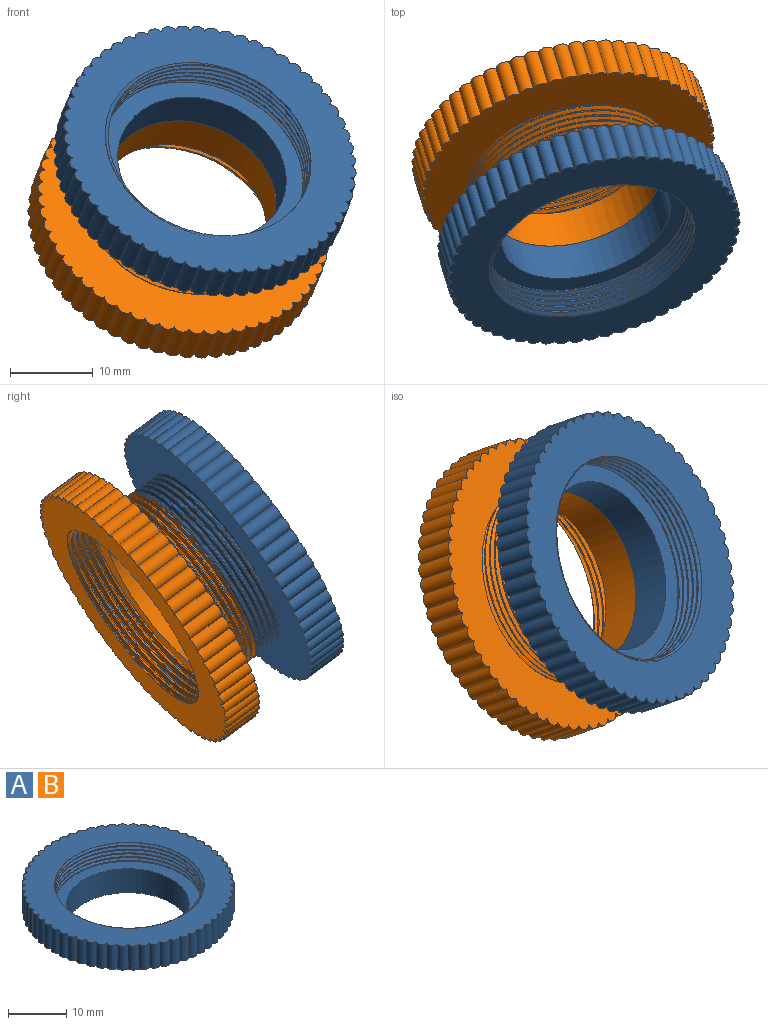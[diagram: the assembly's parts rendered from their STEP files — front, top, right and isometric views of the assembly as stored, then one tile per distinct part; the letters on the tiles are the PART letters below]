
ASSEMBLY  parts=2 mates=1
PART A: 73 faces, bbox 36.8x36.8x10.1 mm
  f0: plane 25.92x25.91mm, normal (0,0,1), area 167.9mm2, adj f4,f9,f10,f11,f12
  f1: plane 36.8x36.8mm, normal (0,0,1), area 507.3mm2, adj f9,f10,f11,f12,f13,f14,f15,f16
  f2: plane 24.63x24.59mm, normal (0,0,-1), area 117.6mm2, adj f3,f4,f6,f7,f8
  f3: cylinder r=12.4mm len=24.8mm, axis (0,0,-1), area 38.2mm2, adj f2,f5,f7,f8
  f4: cylinder r=10.5mm len=21mm, axis (0,0,-1), area 329.9mm2, adj f0,f2
  f5: plane 36.65x36.65mm, normal (0,0,-1), area 557.7mm2, adj f3,f6,f7,f8,f13,f14,f15,f16
  f6: bspline ~27.64x23.94mm, area 84.1mm2, adj f2,f5,f7,f8
  f7: bspline ~28.64x24.8mm, area 191.6mm2, adj f2,f3,f5,f6
  f8: bspline ~28.64x24.8mm, area 191.6mm2, adj f2,f3,f5,f6
  f9: bspline ~26.06x26.05mm, area 201.3mm2, adj f0,f1,f11,f12
  f10: bspline ~30.1x26.07mm, area 201.5mm2, adj f0,f1,f11,f12
  f11: bspline ~30.18x26.14mm, area 47.5mm2, adj f0,f1,f9,f10
  f12: cylinder r=12.6mm len=25.21mm, axis (0,0,1), area 81.8mm2, adj f0,f1,f9,f10
  f13: cylinder r=1mm len=5mm, axis (0,0,-1), area 11.7mm2, adj f1,f5,f14,f72
  f14: cylinder r=1mm len=5mm, axis (0,0,-1), area 11.7mm2, adj f1,f5,f13,f15
  f15: cylinder r=1mm len=5mm, axis (0,0,-1), area 11.7mm2, adj f1,f5,f14,f16
  f16: cylinder r=1mm len=5mm, axis (0,0,-1), area 11.7mm2, adj f1,f5,f15,f17
  f17: cylinder r=1mm len=5mm, axis (0,0,-1), area 11.7mm2, adj f1,f5,f16,f18
  f18: cylinder r=1mm len=5mm, axis (0,0,-1), area 11.7mm2, adj f1,f5,f17,f19
  f19: cylinder r=1mm len=5mm, axis (0,0,-1), area 11.7mm2, adj f1,f5,f18,f20
  f20: cylinder r=1mm len=5mm, axis (0,0,-1), area 11.7mm2, adj f1,f5,f19,f21
  f21: cylinder r=1mm len=5mm, axis (0,0,-1), area 11.7mm2, adj f1,f5,f20,f22
  f22: cylinder r=1mm len=5mm, axis (0,0,-1), area 11.7mm2, adj f1,f5,f21,f23
  f23: cylinder r=1mm len=5mm, axis (0,0,-1), area 11.7mm2, adj f1,f5,f22,f24
  f24: cylinder r=1mm len=5mm, axis (0,0,-1), area 11.7mm2, adj f1,f5,f23,f25
  f25: cylinder r=1mm len=5mm, axis (0,0,-1), area 11.7mm2, adj f1,f5,f24,f26
  f26: cylinder r=1mm len=5mm, axis (0,0,-1), area 11.7mm2, adj f1,f5,f25,f27
  f27: cylinder r=1mm len=5mm, axis (0,0,-1), area 11.7mm2, adj f1,f5,f26,f28
  f28: cylinder r=1mm len=5mm, axis (0,0,-1), area 11.7mm2, adj f1,f5,f27,f29
  f29: cylinder r=1mm len=5mm, axis (0,0,-1), area 11.7mm2, adj f1,f5,f28,f30
  f30: cylinder r=1mm len=5mm, axis (0,0,-1), area 11.7mm2, adj f1,f5,f29,f31
  f31: cylinder r=1mm len=5mm, axis (0,0,-1), area 11.7mm2, adj f1,f5,f30,f32
  f32: cylinder r=1mm len=5mm, axis (0,0,-1), area 11.7mm2, adj f1,f5,f31,f33
  f33: cylinder r=1mm len=5mm, axis (0,0,-1), area 11.7mm2, adj f1,f5,f32,f34
  f34: cylinder r=1mm len=5mm, axis (0,0,-1), area 11.7mm2, adj f1,f5,f33,f35
  f35: cylinder r=1mm len=5mm, axis (0,0,-1), area 11.7mm2, adj f1,f5,f34,f36
  f36: cylinder r=1mm len=5mm, axis (0,0,-1), area 11.7mm2, adj f1,f5,f35,f37
  f37: cylinder r=1mm len=5mm, axis (0,0,-1), area 11.7mm2, adj f1,f5,f36,f38
  f38: cylinder r=1mm len=5mm, axis (0,0,-1), area 11.7mm2, adj f1,f5,f37,f39
  f39: cylinder r=1mm len=5mm, axis (0,0,-1), area 11.7mm2, adj f1,f5,f38,f40
  f40: cylinder r=1mm len=5mm, axis (0,0,-1), area 11.7mm2, adj f1,f5,f39,f41
  f41: cylinder r=1mm len=5mm, axis (0,0,-1), area 11.7mm2, adj f1,f5,f40,f42
  f42: cylinder r=1mm len=5mm, axis (0,0,-1), area 11.7mm2, adj f1,f5,f41,f43
  f43: cylinder r=1mm len=5mm, axis (0,0,-1), area 11.7mm2, adj f1,f5,f42,f44
  f44: cylinder r=1mm len=5mm, axis (0,0,-1), area 11.7mm2, adj f1,f5,f43,f45
  f45: cylinder r=1mm len=5mm, axis (0,0,-1), area 11.7mm2, adj f1,f5,f44,f46
  f46: cylinder r=1mm len=5mm, axis (0,0,-1), area 11.7mm2, adj f1,f5,f45,f47
  f47: cylinder r=1mm len=5mm, axis (0,0,-1), area 11.7mm2, adj f1,f5,f46,f48
  f48: cylinder r=1mm len=5mm, axis (0,0,-1), area 11.7mm2, adj f1,f5,f47,f49
  f49: cylinder r=1mm len=5mm, axis (0,0,-1), area 11.7mm2, adj f1,f5,f48,f50
  f50: cylinder r=1mm len=5mm, axis (0,0,-1), area 11.7mm2, adj f1,f5,f49,f51
  f51: cylinder r=1mm len=5mm, axis (0,0,-1), area 11.7mm2, adj f1,f5,f50,f52
  f52: cylinder r=1mm len=5mm, axis (0,0,-1), area 11.7mm2, adj f1,f5,f51,f53
  f53: cylinder r=1mm len=5mm, axis (0,0,-1), area 11.7mm2, adj f1,f5,f52,f54
  f54: cylinder r=1mm len=5mm, axis (0,0,-1), area 11.7mm2, adj f1,f5,f53,f55
  f55: cylinder r=1mm len=5mm, axis (0,0,-1), area 11.7mm2, adj f1,f5,f54,f56
  f56: cylinder r=1mm len=5mm, axis (0,0,-1), area 11.7mm2, adj f1,f5,f55,f57
  f57: cylinder r=1mm len=5mm, axis (0,0,-1), area 11.7mm2, adj f1,f5,f56,f58
  f58: cylinder r=1mm len=5mm, axis (0,0,-1), area 11.7mm2, adj f1,f5,f57,f59
  f59: cylinder r=1mm len=5mm, axis (0,0,-1), area 11.7mm2, adj f1,f5,f58,f60
  f60: cylinder r=1mm len=5mm, axis (0,0,-1), area 11.7mm2, adj f1,f5,f59,f61
  f61: cylinder r=1mm len=5mm, axis (0,0,-1), area 11.7mm2, adj f1,f5,f60,f62
  f62: cylinder r=1mm len=5mm, axis (0,0,-1), area 11.7mm2, adj f1,f5,f61,f63
  f63: cylinder r=1mm len=5mm, axis (0,0,-1), area 11.7mm2, adj f1,f5,f62,f64
  f64: cylinder r=1mm len=5mm, axis (0,0,-1), area 11.7mm2, adj f1,f5,f63,f65
  f65: cylinder r=1mm len=5mm, axis (0,0,-1), area 11.7mm2, adj f1,f5,f64,f66
  f66: cylinder r=1mm len=5mm, axis (0,0,-1), area 11.7mm2, adj f1,f5,f65,f67
  f67: cylinder r=1mm len=5mm, axis (0,0,-1), area 11.7mm2, adj f1,f5,f66,f68
  f68: cylinder r=1mm len=5mm, axis (0,0,-1), area 11.7mm2, adj f1,f5,f67,f69
  f69: cylinder r=1mm len=5mm, axis (0,0,-1), area 11.7mm2, adj f1,f5,f68,f70
  f70: cylinder r=1mm len=5mm, axis (0,0,-1), area 11.7mm2, adj f1,f5,f69,f71
  f71: cylinder r=1mm len=5mm, axis (0,0,-1), area 11.7mm2, adj f1,f5,f70,f72
  f72: cylinder r=1mm len=5mm, axis (0,0,-1), area 11.7mm2, adj f1,f5,f13,f71
PART B: same geometry as A
PLACE A rot(axis=(0.18,0.51,-0.84),117.1deg) t=(33.52,26.5,-29.46)mm fixed
PLACE B rot(axis=(-0.8,-0.58,-0.17),128.2deg) t=(33.52,26.5,-29.46)mm
MATE cylindrical B.f3 <-> A.f3  axis (0.24,-0.78,0.57) through (33.52,26.5,-29.46)mm
